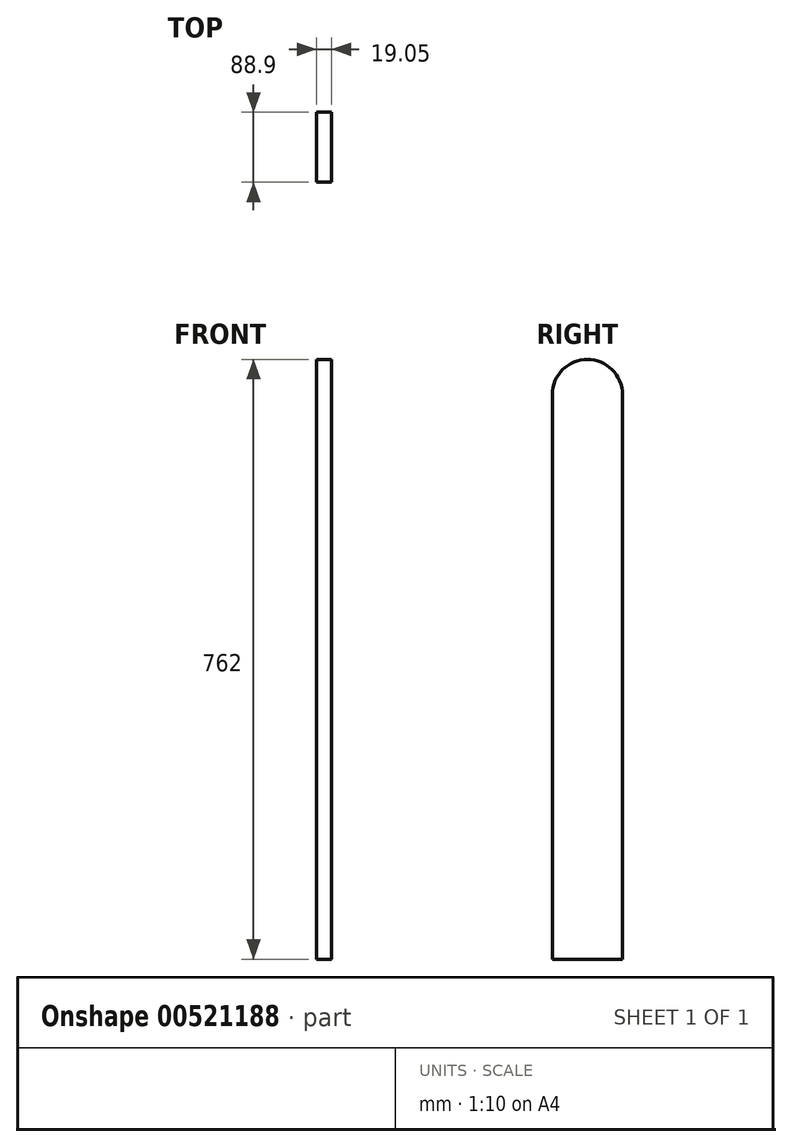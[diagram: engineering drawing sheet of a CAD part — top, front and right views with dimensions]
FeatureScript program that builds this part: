
annotation { "Feature Type Name" : "Feature", "Feature Type Description" : "" }
export const myFeature = defineFeature(function(context is Context, id is Id, definition is map)
    precondition{}
    {
        {
            var Q0;
            Q0=qCreatedBy(makeId("Right.planeOp"),FACE);
            var sketch = newSketch(context, id + "F0", { "sketchPlane" : qUnion([Q0])});
            skLineSegment(sketch, "E0.bottom", {"start": v(0, 0) * mm, "end": v(88.9, 0) * mm});
            skLineSegment(sketch, "E0.top", {"start": v(0, 762) * mm, "end": v(88.9, 762) * mm});
            skLineSegment(sketch, "E0.left", {"start": v(0, 0) * mm, "end": v(0, 762) * mm});
            skLineSegment(sketch, "E0.right", {"start": v(88.9, 0) * mm, "end": v(88.9, 762) * mm});
            skSolve(sketch);
        }
        {
            var Q0;
            Q0=makeQuery(id+"F0.imprint","IMPRINT",FACE,{"disambiguationData":[TD([[makeQuery(id+"F0.imprint","IMPRINT",EDGE,{"derivedFrom":sQuery(id+"F0.wireOp",EDGE,"E0.bottom")}),1.0]])]});
            extrude(context, id + "F1", {"entities" : qUnion([Q0]), "depth" : 19.05 * mm, "offsetDistance" : 25.4 * mm});
        }
        {
            var Q0;
            Q0=makeQuery(id+"F1.opExtrude","SWEPT_EDGE",EDGE,{"disambiguationData":[OSD([sQuery(id+"F0.wireOp",EDGE,"E0.top"),sQuery(id+"F0.wireOp",EDGE,"E0.left")])]});
            var Q1;
            Q1=makeQuery(id+"F1.opExtrude","SWEPT_EDGE",EDGE,{"disambiguationData":[OSD([sQuery(id+"F0.wireOp",EDGE,"E0.top"),sQuery(id+"F0.wireOp",EDGE,"E0.right")])]});
            fillet(context, id + "F2", {"entities" : qUnion([Q0, Q1]), "radius" : 44.45 * mm, "tangentPropagation" : true, "allowEdgeOverflow" : false});
        }
    });
